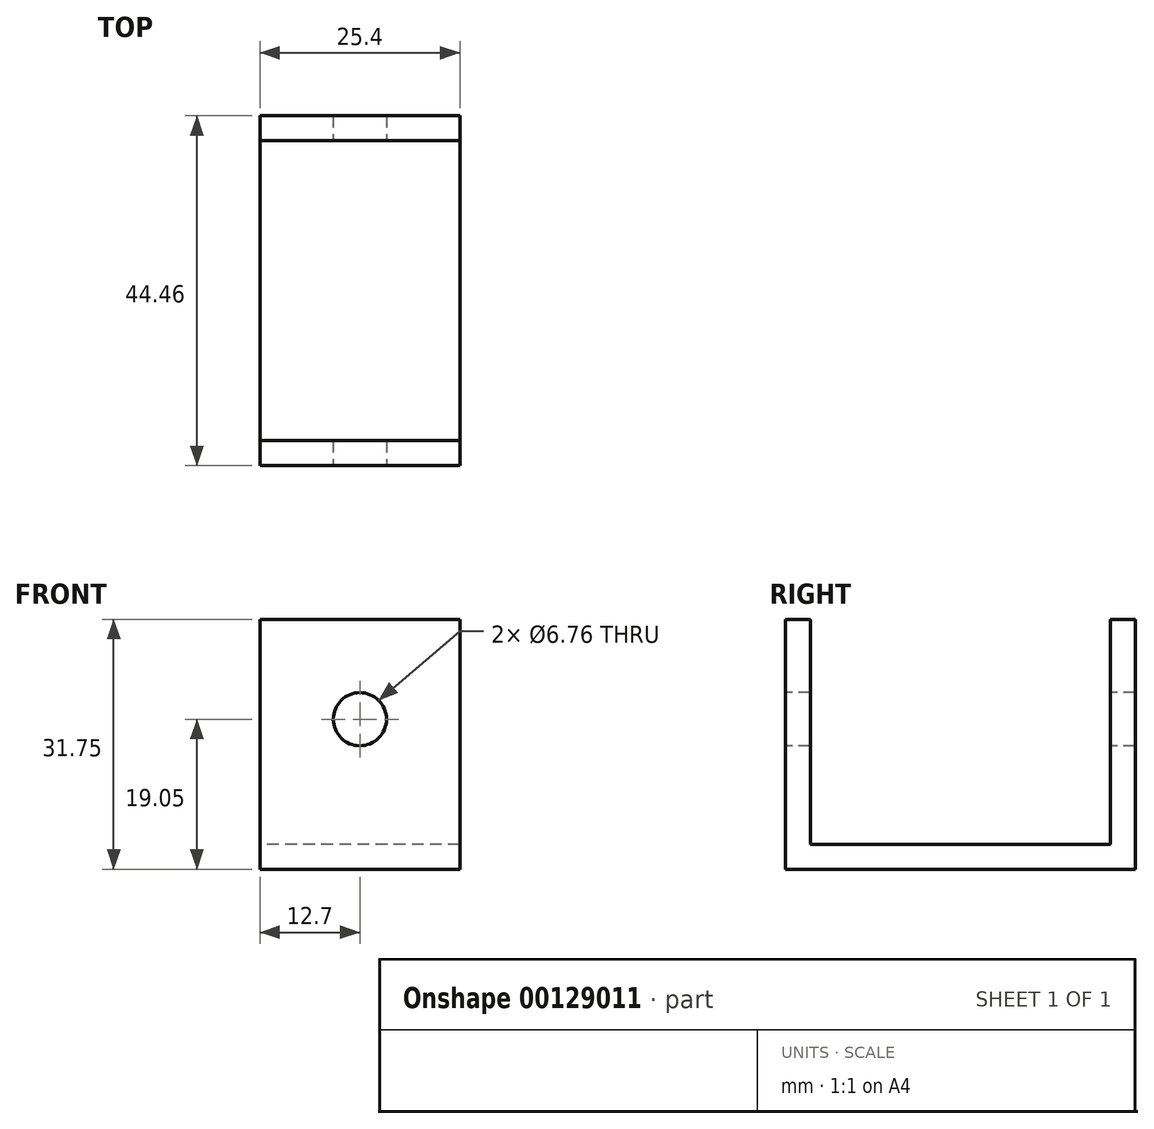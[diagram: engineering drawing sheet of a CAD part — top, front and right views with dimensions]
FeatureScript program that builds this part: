
annotation { "Feature Type Name" : "Feature", "Feature Type Description" : "" }
export const myFeature = defineFeature(function(context is Context, id is Id, definition is map)
    precondition{}
    {
        {
            var Q0;
            Q0=qCreatedBy(makeId("Right.planeOp"),FACE);
            var sketch = newSketch(context, id + "F0", { "sketchPlane" : qUnion([Q0])});
            skLineSegment(sketch, "E0", {"start": v(-22.22, 0) * mm, "end": v(22.22, 0) * mm});
            skLineSegment(sketch, "E1", {"start": v(22.22, 0) * mm, "end": v(22.22, 31.75) * mm});
            skLineSegment(sketch, "E2", {"start": v(22.22, 31.75) * mm, "end": v(19.05, 31.75) * mm});
            skLineSegment(sketch, "E3", {"start": v(19.05, 31.75) * mm, "end": v(19.05, 3.18) * mm});
            skLineSegment(sketch, "E4", {"start": v(19.05, 3.18) * mm, "end": v(-19.05, 3.18) * mm});
            skLineSegment(sketch, "E5", {"start": v(-19.05, 3.18) * mm, "end": v(-19.05, 31.75) * mm});
            skLineSegment(sketch, "E6", {"start": v(-19.05, 31.75) * mm, "end": v(-22.23, 31.75) * mm});
            skLineSegment(sketch, "E7", {"start": v(-22.23, 31.75) * mm, "end": v(-22.22, 0) * mm});
            skLineSegment(sketch, "E8", {"start": v(0, 3.18) * mm, "end": v(0, 0) * mm});
            skSolve(sketch);
        }
        {
            var Q0;
            {var subQ0=sQuery(id+"F0.wireOp",EDGE,"E5");Q0=makeQuery(id+"F0.imprint","IMPRINT",FACE,{"disambiguationData":[TD([[makeQuery(id+"F0.imprint","IMPRINT",EDGE,{"derivedFrom":subQ0}),1.0]])]});}
            var Q1;
            {var subQ2=sQuery(id+"F0.wireOp",EDGE,"E1");Q1=makeQuery(id+"F0.imprint","IMPRINT",FACE,{"disambiguationData":[TD([[makeQuery(id+"F0.imprint","IMPRINT",EDGE,{"derivedFrom":subQ2}),1.0]])]});}
            extrude(context, id + "F1", {"entities" : qUnion([Q0, Q1]), "endBound" : BoundingType.SYMMETRIC, "depth" : 25.4 * mm});
        }
        {
            var Q0;
            Q0=makeQuery(id+"F1.opExtrude","SWEPT_FACE",FACE,{"disambiguationData":[OSD([sQuery(id+"F0.wireOp",EDGE,"E7")])]});
            var sketch = newSketch(context, id + "F2", { "sketchPlane" : qUnion([Q0])});
            skPoint(sketch, "E9", {"position": v(0, 19.05) * mm});
            skSolve(sketch);
        }
        {
            var Q0;
            Q0=sQuery(id+"F2.wireOp",VERTEX,"E9");
            var Q1;
            Q1=makeQuery(id+"F1.opExtrude","SWEPT_BODY",BODY,{"disambiguationData":[OSD([sQuery(id+"F0.wireOp",EDGE,"E0"),sQuery(id+"F0.wireOp",EDGE,"E1"),sQuery(id+"F0.wireOp",EDGE,"E2"),sQuery(id+"F0.wireOp",EDGE,"E3"),sQuery(id+"F0.wireOp",EDGE,"E4"),sQuery(id+"F0.wireOp",EDGE,"E5"),sQuery(id+"F0.wireOp",EDGE,"E6"),sQuery(id+"F0.wireOp",EDGE,"E7")])]});
            hole(context, id + "F3", {"style" : HoleStyle.SIMPLE, "endStyle" : HoleEndStyle.THROUGH, "standardTappedOrClearance" : lookupTablePath({ "standard" : "ANSI", "fit" : "Normal (ASME)", "size" : "1/4", "type" : "Clearance" }), "standardBlindInLast" : lookupTablePath({ "fit" : "Free", "standard" : "ANSI", "size" : "1/4", "type" : "Clearance" }), "holeDiameter" : 6.76 * mm, "locations" : qUnion([Q0]), "scope" : qUnion([Q1]), "isTappedThrough" : true});
        }
    });
